# Revit family: 90002106 - Aventa Silent AVS 315 - BIM file
name_source: partatom
category: Mechanical Equipment
units: mm (PartAtom-declared; Revit-internal decimal feet)

## family parameters
Always vertical = No
Classification = None
Cut with Voids When Loaded = No
Maintain Annotation Orientation = No
OmniClass Number = 23.75.35.17.11
OmniClass Title = Fans for Air Ductwork
Part Type = Breaks Into
Room Calculation Point = No
Round Connector Dimension = Use Diameter
Shared = No
Work Plane-Based = No

## types (2) — shared parameters
Current = 1 A
D = 315 mm  [stored 1.03346 ft]
D1 = 432 mm  [stored 1.41732 ft]
Dd12 = 1 mm  [stored 0.00328084 ft]
Dd13 = 2 mm  [stored 0.00656168 ft]
Dd14 = 6 mm  [stored 0.019685 ft]
Dd16 = 55 mm  [stored 0.180446 ft]
Dd22 = 5 mm  [stored 0.0164042 ft]
Dd23 = 6 mm  [stored 0.019685 ft]
Dd24 = 30 mm  [stored 0.0984252 ft]
Dd26 = 52 mm
Description = Inline mixed-flow fan suitable for domestic and light commercial facilities
Dimensions = (H) 434 x (W) 780 x (D) 520mm
Distribution Box Material = Distribution Box Dark Grey
Duct Connection Size = 315 mm  [stored 1.03346 ft]
ElBoxH = 53 mm  [stored 0.173885 ft]
ElBoxL = 104 mm
ElBoxR = 15 mm  [stored 0.0492126 ft]
ElBoxW = 104 mm
Family Version = 1.0
Fan Material = Metal Black
Hanger Material = Metal Zinc
HangerBaseH = 219 mm  [stored 0.718504 ft]
HangerExtraL = No
HangerH = 219 mm  [stored 0.718504 ft]
HangerL = 478 mm  [stored 1.56824 ft]
HangerL1 = 396 mm  [stored 1.29921 ft]
HangerW = 200 mm  [stored 0.656168 ft]
L = 780 mm  [stored 2.55906 ft]
L1 = 32 mm  [stored 0.104987 ft]
L11 = 195 mm  [stored 0.639764 ft]
L12 = 8 mm  [stored 0.0262467 ft]
L13 = 8 mm  [stored 0.0262467 ft]
L14 = 10 mm  [stored 0.0328084 ft]
L15 = 153 mm  [stored 0.501969 ft]
L16 = 6 mm  [stored 0.019685 ft]
L17 = 10 mm  [stored 0.0328084 ft]
L2 = 32 mm  [stored 0.104987 ft]
L21 = 218 mm  [stored 0.715223 ft]
L22 = 8 mm  [stored 0.0262467 ft]
L23 = 13 mm
L24 = 27 mm  [stored 0.0885827 ft]
L25 = 154 mm
L26 = 6 mm  [stored 0.019685 ft]
L27 = 10 mm  [stored 0.0328084 ft]
Load Classification = HVAC
Maintenance Zone Height = 600 mm  [stored 1.9685 ft]
Maintenance Zone Length = 600 mm  [stored 1.9685 ft]
Maintenance Zone Length Calc = 780 mm  [stored 2.55906 ft]
Maintenance Zone Material = Maintenance Zone
Maintenance Zone Width = 600 mm  [stored 1.9685 ft]
Manufacturer = Airflow
Material finish = Polymer Coated Steel
Number of Poles = 1
Power Factor = 1
Protection rating = IPX4
R1 = 216 mm  [stored 0.708661 ft]
RPM (min-1) = 2430
Transported Air Temperature (°C) = -25...+60
URL = https://www.airflow.com
Weight = 25.00 kg
zero-valued in all types: Default Elevation

## per-type parameters (varying)
| type | Airflow part no | Apparent Power | Maximum Air Flow | Model | Noise Level at 3 m (dBa) | Power | Type Comments | Voltage |
| Aventa Silent AVS315 Basic | 90002106 | 230 VA | 1570 m³/h | Aventa Silent AVS315 Basic | 36 | 230 W | Inline fan single speed up to 1570m3/h | 230 V |
| Aventa Silent AV315 Timer | 90002123 | 330 VA | 2050 m³/h | Aventa Silent AVS315 Timer | 40 | 330 W | Inline fan single speed up to 2050m3/h | 330 V |

note: [stored X ft] marks values corroborated as IEEE doubles in the binary element streams (Revit-internal decimal feet)

## geometry (parser evidence)
native form markers: Sweep x11
no freeform markers — native parametric forms only
